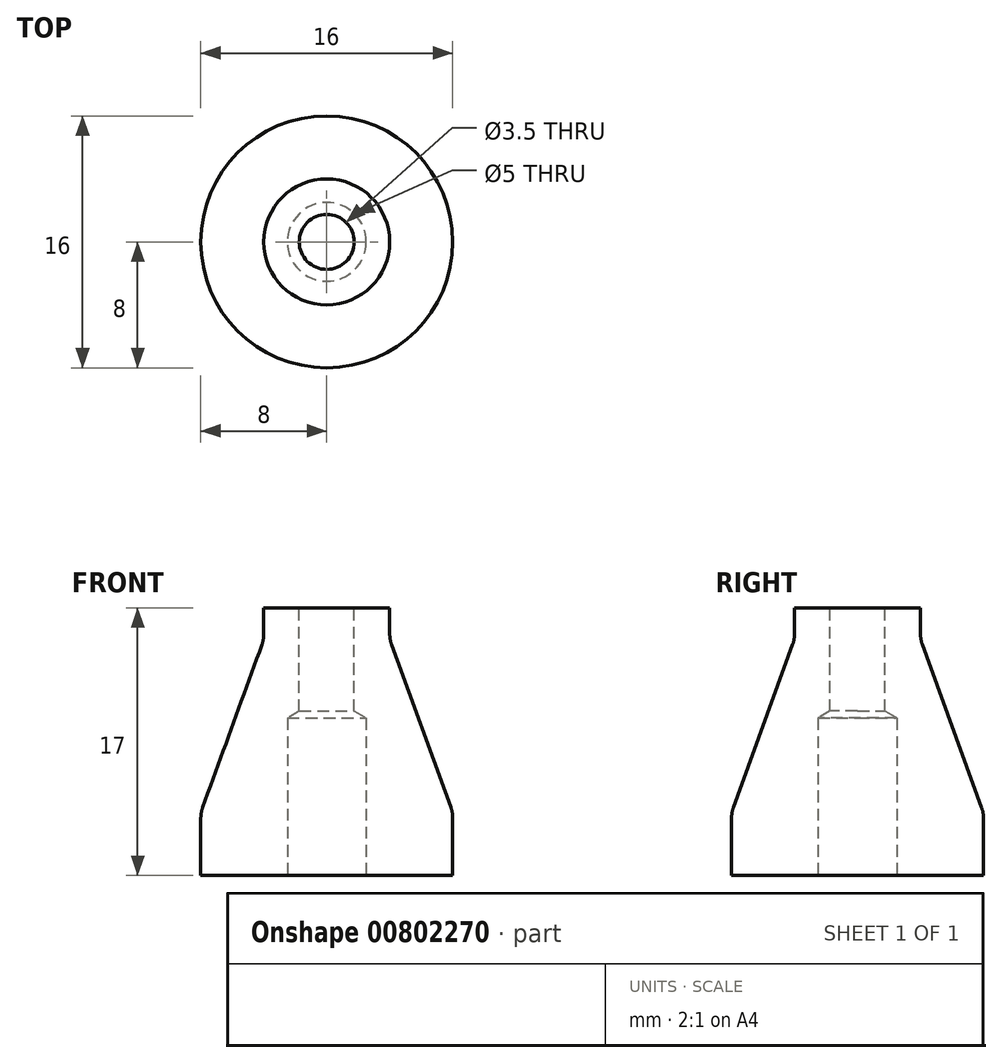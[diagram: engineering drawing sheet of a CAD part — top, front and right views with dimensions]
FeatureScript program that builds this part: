
annotation { "Feature Type Name" : "Feature", "Feature Type Description" : "" }
export const myFeature = defineFeature(function(context is Context, id is Id, definition is map)
    precondition{}
    {
        {
            var Q0;
            Q0=qCreatedBy(makeId("Top.planeOp"),FACE);
            var sketch = newSketch(context, id + "F0", { "sketchPlane" : qUnion([Q0])});
            skCircle(sketch, "E0", {"center": v(0, 0) * mm, "radius": 8 * mm});
            skSolve(sketch);
        }
        {
            var Q0;
            Q0=makeQuery(id+"F0.imprint","IMPRINT",FACE,{"disambiguationData":[TD([[makeQuery(id+"F0.imprint","IMPRINT",EDGE,{"derivedFrom":sQuery(id+"F0.wireOp",EDGE,"E0")}),1.0]])]});
            extrude(context, id + "F1", {"entities" : qUnion([Q0]), "depth" : 17 * mm, "offsetDistance" : 25 * mm});
        }
        {
            var Q0;
            Q0=qCreatedBy(makeId("Right.planeOp"),FACE);
            var sketch = newSketch(context, id + "F2", { "sketchPlane" : qUnion([Q0])});
            skLineSegment(sketch, "E1", {"start": v(8, 4) * mm, "end": v(4, 15) * mm});
            skLineSegment(sketch, "E2", {"start": v(8, 17) * mm, "end": v(8, 0) * mm});
            skLineSegment(sketch, "E3", {"start": v(4, 15) * mm, "end": v(4, 17) * mm});
            skLineSegment(sketch, "E4", {"start": v(4, 17) * mm, "end": v(8, 17) * mm});
            skLineSegment(sketch, "E5", {"start": v(0, 0) * mm, "end": v(0, 18.4) * mm});
            skSolve(sketch);
        }
        {
            var Q0;
            Q0 = qSketchRegion(id + "F2", true);
            var Q1;
            Q1=sQuery(id+"F2.wireOp",EDGE,"E5");
            revolve(context, id + "F3", {"operationType" : NewBodyOperationType.REMOVE, "surfaceOperationType" : NewSurfaceOperationType.NEW, "entities" : qUnion([Q0]), "axis" : qUnion([Q1]), "revolveType" : RevolveType.FULL});
        }
        {
            var Q0;
            Q0=makeQuery(id+"F1.opExtrude","CAP_FACE",FACE,{"disambiguationData":[OSD([sQuery(id+"F0.wireOp",EDGE,"E0")])],"isStart":false});
            var sketch = newSketch(context, id + "F4", { "sketchPlane" : qUnion([Q0])});
            skPoint(sketch, "E6", {"position": v(0, 0) * mm});
            skSolve(sketch);
        }
        {
            var Q0;
            Q0=sQuery(id+"F4.wireOp",VERTEX,"E6");
            var Q1;
            Q1=makeQuery(id+"F1.opExtrude","SWEPT_BODY",BODY,{"disambiguationData":[OSD([sQuery(id+"F0.wireOp",EDGE,"E0")])]});
            hole(context, id + "F5", {"style" : HoleStyle.SIMPLE, "endStyle" : HoleEndStyle.THROUGH, "standardTappedOrClearance" : lookupTablePath({ "standard" : "ISO", "engagement" : "50%", "pitch" : "0.7 mm", "size" : "M4", "type" : "Tapped" }), "standardBlindInLast" : lookupTablePath({ "standard" : "ISO", "engagement" : "50%", "pitch" : "0.7 mm", "size" : "M4", "type" : "Tapped" }), "holeDiameter" : 3.5 * mm, "majorDiameter" : 4 * mm, "showTappedDepth" : true, "tappedDepth" : 5 * mm, "tapClearance" : 3, "locations" : qUnion([Q0]), "scope" : qUnion([Q1])});
        }
        {
            var Q0;
            Q0=makeQuery(id+"F1.opExtrude","CAP_FACE",FACE,{"disambiguationData":[OSD([sQuery(id+"F0.wireOp",EDGE,"E0")])],"isStart":true});
            var sketch = newSketch(context, id + "F6", { "sketchPlane" : qUnion([Q0])});
            skPoint(sketch, "E7", {"position": v(0, 0) * mm});
            skSolve(sketch);
        }
        {
            var Q0;
            Q0=sQuery(id+"F6.wireOp",VERTEX,"E7");
            var Q1;
            Q1=makeQuery(id+"F1.opExtrude","SWEPT_BODY",BODY,{"disambiguationData":[OSD([sQuery(id+"F0.wireOp",EDGE,"E0")])]});
            hole(context, id + "F7", {"style" : HoleStyle.SIMPLE, "endStyle" : HoleEndStyle.BLIND, "standardTappedOrClearance" : lookupTablePath({ "standard" : "ISO", "engagement" : "75%", "pitch" : "1 mm", "size" : "M6", "type" : "Tapped" }), "standardBlindInLast" : lookupTablePath({ "standard" : "ISO", "engagement" : "75%", "pitch" : "1 mm", "size" : "M6", "type" : "Tapped" }), "holeDiameter" : 5 * mm, "majorDiameter" : 6 * mm, "showTappedDepth" : true, "holeDepth" : 10 * mm, "isTappedThrough" : true, "tappedDepth" : 7 * mm, "tapClearance" : 3, "locations" : qUnion([Q0]), "scope" : qUnion([Q1])});
        }
        {
            var Q0;
            Q0=makeQuery(id+"F3.boolean.opBoolean","COPY",FACE,{"derivedFrom":makeQuery(id+"F3.opRevolve","SWEPT_FACE",FACE,{"disambiguationData":[OSD([sQuery(id+"F2.wireOp",EDGE,"E1")])]})});
            fillet(context, id + "F8", {"entities" : qUnion([Q0]), "radius" : 2 * mm, "tangentPropagation" : true, "allowEdgeOverflow" : false});
        }
    });
